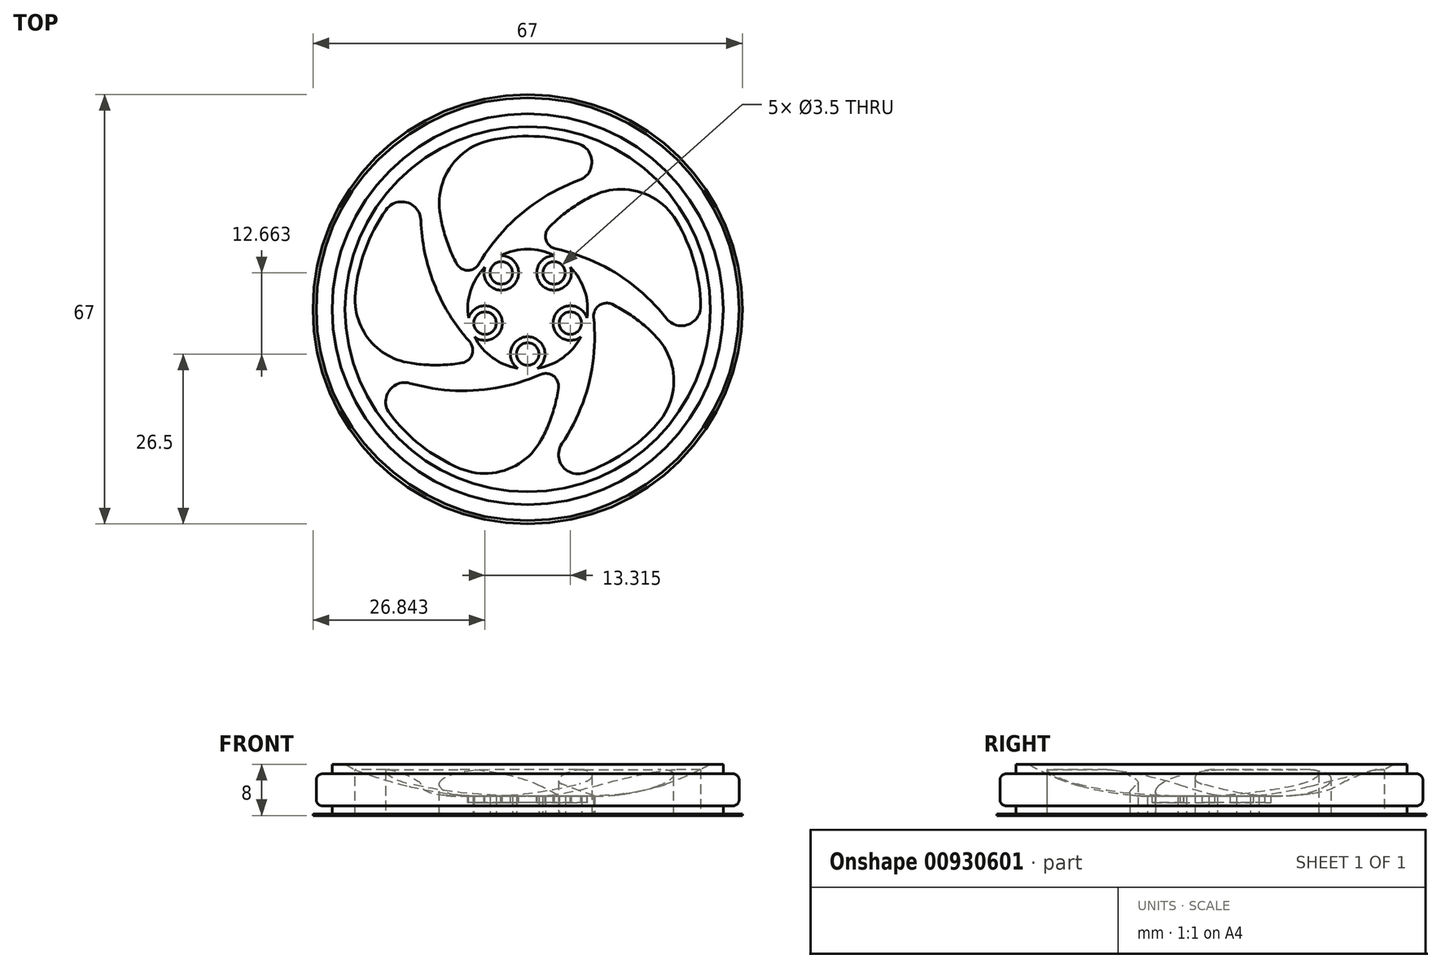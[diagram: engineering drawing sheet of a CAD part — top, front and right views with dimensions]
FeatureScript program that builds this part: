
annotation { "Feature Type Name" : "Feature", "Feature Type Description" : "" }
export const myFeature = defineFeature(function(context is Context, id is Id, definition is map)
    precondition{}
    {
        {
            var Q0;
            Q0=qCreatedBy(makeId("Front.planeOp"),FACE);
            var sketch = newSketch(context, id + "F0", { "sketchPlane" : qUnion([Q0])});
            skLineSegment(sketch, "E0.right", {"start": v(33, 1.5) * mm, "end": v(33, 6.5) * mm});
            skLineSegment(sketch, "E1", {"start": v(30.5, 6.5) * mm, "end": v(33, 6.5) * mm});
            skLineSegment(sketch, "E2", {"start": v(30.5, 6.5) * mm, "end": v(30.5, 8) * mm});
            skLineSegment(sketch, "E3.MirrorCS", {"start": v(30.5, 1.5) * mm, "end": v(30.5, 0) * mm});
            skLineSegment(sketch, "E4.MirrorCS", {"start": v(30.5, 1.5) * mm, "end": v(33, 1.5) * mm});
            skLineSegment(sketch, "E5.trimOffspring", {"start": v(28.5, 8) * mm, "end": v(30.5, 8) * mm});
            skLineSegment(sketch, "E6", {"start": v(0, 0) * mm, "end": v(30.5, 0) * mm});
            skLineSegment(sketch, "E7", {"start": v(0, 0) * mm, "end": v(0, 3) * mm});
            skLineSegment(sketch, "E8", {"start": v(0, 3) * mm, "end": v(10, 3) * mm});
            skArc(sketch, "E9", {"start": v(10, 3) * mm, "mid": v(19.58, 4.27) * mm, "end": v(28.5, 8) * mm});
            skSolve(sketch);
        }
        {
            var Q0;
            Q0=qSketchRegion(id+"F0",true);
            var Q1;
            Q1=sQuery(id+"F0.wireOp",EDGE,"E7");
            revolve(context, id + "F1", {"entities" : qUnion([Q0]), "axis" : qUnion([Q1]), "revolveType" : RevolveType.FULL});
        }
        {
            var Q0;
            Q0=makeQuery(id+"F1.opRevolve","SWEPT_EDGE",EDGE,{"disambiguationData":[OSD([sQuery(id+"F0.wireOp",EDGE,"E0.right"),sQuery(id+"F0.wireOp",EDGE,"E1")])]});
            var Q1;
            Q1=makeQuery(id+"F1.opRevolve","SWEPT_EDGE",EDGE,{"disambiguationData":[OSD([sQuery(id+"F0.wireOp",EDGE,"E0.right"),sQuery(id+"F0.wireOp",EDGE,"E4.MirrorCS")])]});
            fillet(context, id + "F2", {"entities" : qUnion([Q0, Q1]), "radius" : 1 * mm, "tangentPropagation" : true, "allowEdgeOverflow" : false});
        }
        {
            var Q0;
            Q0=makeQuery(id+"F1.opRevolve","SWEPT_FACE",FACE,{"disambiguationData":[OSD([sQuery(id+"F0.wireOp",EDGE,"E6")])]});
            var sketch = newSketch(context, id + "F3", { "sketchPlane" : qUnion([Q0])});
            skCircle(sketch, "E10", {"center": v(0, 0) * mm, "radius": 10 * mm, "construction": true});
            skCircle(sketch, "E11", {"center": v(0, 0) * mm, "radius": 28.5 * mm, "construction": true});
            skArc(sketch, "E12", {"start": v(-3, 26.83) * mm, "mid": v(-17.06, 20.93) * mm, "end": v(-25.68, 8.34) * mm});
            skArc(sketch, "E13.trimOffspring", {"start": v(-26.45, 5.44) * mm, "mid": v(-25.18, -9.76) * mm, "end": v(-15.87, -21.84) * mm});
            skArc(sketch, "E14.trimOffspring", {"start": v(18.2, -19.95) * mm, "mid": v(26.1, -6.9) * mm, "end": v(25.68, 8.34) * mm});
            skLineSegment(sketch, "E15", {"start": v(0, 28.5) * mm, "end": v(0, 0) * mm, "construction": true});
            skLineSegment(sketch, "E16", {"start": v(0, 0) * mm, "end": v(-25.68, 8.34) * mm, "construction": true});
            skLineSegment(sketch, "E17", {"start": v(0, 0) * mm, "end": v(25.68, 8.34) * mm, "construction": true});
            skLineSegment(sketch, "E18", {"start": v(0, 0) * mm, "end": v(-15.87, -21.84) * mm, "construction": true});
            skLineSegment(sketch, "E19", {"start": v(0, 0) * mm, "end": v(15.87, -21.84) * mm, "construction": true});
            skArc(sketch, "E20.trimOffspring", {"start": v(24.6, 11.14) * mm, "mid": v(14.63, 22.7) * mm, "end": v(0, 27) * mm});
            skArc(sketch, "E21.trimOffspring", {"start": v(-13.35, -23.47) * mm, "mid": v(1.5, -26.96) * mm, "end": v(15.87, -21.84) * mm});
            skCircle(sketch, "E22", {"center": v(0, 7) * mm, "radius": 1.75 * mm});
            skCircle(sketch, "E23", {"center": v(-4.11, -5.66) * mm, "radius": 1.75 * mm});
            skCircle(sketch, "E24", {"center": v(4.11, -5.66) * mm, "radius": 1.75 * mm});
            skCircle(sketch, "E25", {"center": v(6.66, 2.16) * mm, "radius": 1.75 * mm});
            skCircle(sketch, "E26", {"center": v(-6.66, 2.16) * mm, "radius": 1.75 * mm});
            skArc(sketch, "E27", {"start": v(9.77, -2.12) * mm, "mid": v(8.9, 13.79) * mm, "end": v(0, 27) * mm});
            skArc(sketch, "E28", {"start": v(1, -9.95) * mm, "mid": v(15.86, -4.2) * mm, "end": v(25.68, 8.34) * mm});
            skArc(sketch, "E29", {"start": v(-9.15, -4.03) * mm, "mid": v(0.9, -16.38) * mm, "end": v(15.87, -21.84) * mm});
            skArc(sketch, "E30", {"start": v(-6.66, 7.46) * mm, "mid": v(-15.3, -5.92) * mm, "end": v(-15.87, -21.84) * mm});
            skArc(sketch, "E31", {"start": v(5.04, 8.64) * mm, "mid": v(-10.36, 12.72) * mm, "end": v(-25.68, 8.34) * mm});
            skArc(sketch, "E32", {"start": v(-6.66, 7.46) * mm, "mid": v(-16.77, 8.6) * mm, "end": v(-26.45, 5.44) * mm});
            skArc(sketch, "E33", {"start": v(5.04, 8.64) * mm, "mid": v(3, 18.6) * mm, "end": v(-3, 26.83) * mm});
            skArc(sketch, "E34", {"start": v(9.77, -2.12) * mm, "mid": v(18.62, 2.9) * mm, "end": v(24.6, 11.14) * mm});
            skArc(sketch, "E35", {"start": v(1, -9.95) * mm, "mid": v(8.52, -16.81) * mm, "end": v(18.2, -19.95) * mm});
            skArc(sketch, "E36", {"start": v(-9.15, -4.03) * mm, "mid": v(-13.36, -13.3) * mm, "end": v(-13.35, -23.47) * mm});
            skSolve(sketch);
        }
        {
            var Q0;
            Q0=qSketchRegion(id+"F3",true);
            extrude(context, id + "F4", {"entities" : qUnion([Q0]), "operationType" : NewBodyOperationType.REMOVE, "oppositeDirection" : true, "depth" : 25 * mm});
        }
        {
            var Q0;
            Q0=makeQuery(id+"F4.boolean.opBoolean","COPY",EDGE,{"derivedFrom":makeQuery(id+"F4.opExtrude","SWEPT_EDGE",EDGE,{"disambiguationData":[OSD([sQuery(id+"F3.wireOp",EDGE,"E20.trimOffspring"),sQuery(id+"F3.wireOp",EDGE,"E27")])]})});
            var Q1;
            Q1=makeQuery(id+"F4.boolean.opBoolean","COPY",EDGE,{"derivedFrom":makeQuery(id+"F4.opExtrude","SWEPT_EDGE",EDGE,{"disambiguationData":[OSD([sQuery(id+"F3.wireOp",EDGE,"E12"),sQuery(id+"F3.wireOp",EDGE,"E31")])]})});
            var Q2;
            Q2=makeQuery(id+"F4.boolean.opBoolean","COPY",EDGE,{"derivedFrom":makeQuery(id+"F4.opExtrude","SWEPT_EDGE",EDGE,{"disambiguationData":[OSD([sQuery(id+"F3.wireOp",EDGE,"E13.trimOffspring"),sQuery(id+"F3.wireOp",EDGE,"E30")])]})});
            var Q3;
            Q3=makeQuery(id+"F4.boolean.opBoolean","COPY",EDGE,{"derivedFrom":makeQuery(id+"F4.opExtrude","SWEPT_EDGE",EDGE,{"disambiguationData":[OSD([sQuery(id+"F3.wireOp",EDGE,"E21.trimOffspring"),sQuery(id+"F3.wireOp",EDGE,"E29")])]})});
            var Q4;
            Q4=makeQuery(id+"F4.boolean.opBoolean","COPY",EDGE,{"derivedFrom":makeQuery(id+"F4.opExtrude","SWEPT_EDGE",EDGE,{"disambiguationData":[OSD([sQuery(id+"F3.wireOp",EDGE,"E14.trimOffspring"),sQuery(id+"F3.wireOp",EDGE,"E28")])]})});
            fillet(context, id + "F5", {"entities" : qUnion([Q0, Q1, Q2, Q3, Q4]), "radius" : 3 * mm, "tangentPropagation" : true, "allowEdgeOverflow" : false});
        }
        {
            var Q0;
            Q0=makeQuery(id+"F4.boolean.opBoolean","COPY",EDGE,{"derivedFrom":makeQuery(id+"F4.opExtrude","SWEPT_EDGE",EDGE,{"disambiguationData":[OSD([sQuery(id+"F3.wireOp",EDGE,"E14.trimOffspring"),sQuery(id+"F3.wireOp",EDGE,"E35")])]})});
            var Q1;
            Q1=makeQuery(id+"F4.boolean.opBoolean","COPY",EDGE,{"derivedFrom":makeQuery(id+"F4.opExtrude","SWEPT_EDGE",EDGE,{"disambiguationData":[OSD([sQuery(id+"F3.wireOp",EDGE,"E20.trimOffspring"),sQuery(id+"F3.wireOp",EDGE,"E34")])]})});
            var Q2;
            Q2=makeQuery(id+"F4.boolean.opBoolean","COPY",EDGE,{"derivedFrom":makeQuery(id+"F4.opExtrude","SWEPT_EDGE",EDGE,{"disambiguationData":[OSD([sQuery(id+"F3.wireOp",EDGE,"E12"),sQuery(id+"F3.wireOp",EDGE,"E33")])]})});
            var Q3;
            Q3=makeQuery(id+"F4.boolean.opBoolean","COPY",EDGE,{"derivedFrom":makeQuery(id+"F4.opExtrude","SWEPT_EDGE",EDGE,{"disambiguationData":[OSD([sQuery(id+"F3.wireOp",EDGE,"E13.trimOffspring"),sQuery(id+"F3.wireOp",EDGE,"E32")])]})});
            var Q4;
            Q4=makeQuery(id+"F4.boolean.opBoolean","COPY",EDGE,{"derivedFrom":makeQuery(id+"F4.opExtrude","SWEPT_EDGE",EDGE,{"disambiguationData":[OSD([sQuery(id+"F3.wireOp",EDGE,"E21.trimOffspring"),sQuery(id+"F3.wireOp",EDGE,"E36")])]})});
            fillet(context, id + "F6", {"entities" : qUnion([Q0, Q1, Q2, Q3, Q4]), "radius" : 10 * mm, "tangentPropagation" : true, "allowEdgeOverflow" : false});
        }
        {
            var Q0;
            Q0=makeQuery(id+"F4.boolean.opBoolean","COPY",EDGE,{"derivedFrom":makeQuery(id+"F4.opExtrude","SWEPT_EDGE",EDGE,{"disambiguationData":[OSD([sQuery(id+"F3.wireOp",EDGE,"E30"),sQuery(id+"F3.wireOp",EDGE,"E32")])]})});
            var Q1;
            Q1=makeQuery(id+"F4.boolean.opBoolean","COPY",EDGE,{"derivedFrom":makeQuery(id+"F4.opExtrude","SWEPT_EDGE",EDGE,{"disambiguationData":[OSD([sQuery(id+"F3.wireOp",EDGE,"E29"),sQuery(id+"F3.wireOp",EDGE,"E36")])]})});
            var Q2;
            Q2=makeQuery(id+"F4.boolean.opBoolean","COPY",EDGE,{"derivedFrom":makeQuery(id+"F4.opExtrude","SWEPT_EDGE",EDGE,{"disambiguationData":[OSD([sQuery(id+"F3.wireOp",EDGE,"E28"),sQuery(id+"F3.wireOp",EDGE,"E35")])]})});
            var Q3;
            Q3=makeQuery(id+"F4.boolean.opBoolean","COPY",EDGE,{"derivedFrom":makeQuery(id+"F4.opExtrude","SWEPT_EDGE",EDGE,{"disambiguationData":[OSD([sQuery(id+"F3.wireOp",EDGE,"E27"),sQuery(id+"F3.wireOp",EDGE,"E34")])]})});
            var Q4;
            Q4=makeQuery(id+"F4.boolean.opBoolean","COPY",EDGE,{"derivedFrom":makeQuery(id+"F4.opExtrude","SWEPT_EDGE",EDGE,{"disambiguationData":[OSD([sQuery(id+"F3.wireOp",EDGE,"E31"),sQuery(id+"F3.wireOp",EDGE,"E33")])]})});
            fillet(context, id + "F7", {"entities" : qUnion([Q0, Q1, Q2, Q3, Q4]), "radius" : 2 * mm, "tangentPropagation" : true, "allowEdgeOverflow" : false});
        }
        {
            var Q0;
            Q0=makeQuery(id+"F1.opRevolve","SWEPT_FACE",FACE,{"disambiguationData":[OSD([sQuery(id+"F0.wireOp",EDGE,"E8")])]});
            var sketch = newSketch(context, id + "F8", { "sketchPlane" : qUnion([Q0])});
            skArc(sketch, "E37", {"start": v(-6.66, 6.56) * mm, "mid": v(-2.53, 3.48) * mm, "end": v(-4.18, 8.36) * mm});
            skArc(sketch, "E38", {"start": v(4.18, 8.36) * mm, "mid": v(2.53, 3.48) * mm, "end": v(6.66, 6.56) * mm});
            skArc(sketch, "E39", {"start": v(9.25, -1.4) * mm, "mid": v(4.09, -1.33) * mm, "end": v(8.3, -4.3) * mm});
            skArc(sketch, "E40", {"start": v(1.53, -9.22) * mm, "mid": v(0, -4.3) * mm, "end": v(-1.53, -9.22) * mm});
            skArc(sketch, "E41", {"start": v(-8.3, -4.3) * mm, "mid": v(-4.09, -1.33) * mm, "end": v(-9.25, -1.4) * mm});
            skArc(sketch, "E42", {"start": v(-6.66, 6.56) * mm, "mid": v(-8.9, 2.89) * mm, "end": v(-9.25, -1.4) * mm});
            skArc(sketch, "E43.trimOffspring", {"start": v(4.18, 8.36) * mm, "mid": v(0, 9.35) * mm, "end": v(-4.18, 8.36) * mm});
            skArc(sketch, "E44.trimOffspring", {"start": v(9.25, -1.4) * mm, "mid": v(8.9, 2.89) * mm, "end": v(6.66, 6.56) * mm});
            skArc(sketch, "E45.trimOffspring", {"start": v(1.53, -9.22) * mm, "mid": v(5.5, -7.56) * mm, "end": v(8.3, -4.3) * mm});
            skArc(sketch, "E46.trimOffspring", {"start": v(-8.3, -4.3) * mm, "mid": v(-5.5, -7.56) * mm, "end": v(-1.53, -9.22) * mm});
            skSolve(sketch);
        }
        {
            var Q0;
            Q0=qSketchRegion(id+"F8",true);
            extrude(context, id + "F9", {"entities" : qUnion([Q0]), "operationType" : NewBodyOperationType.REMOVE, "oppositeDirection" : true, "depth" : 1 * mm});
        }
        {
            var Q0;
            Q0=makeQuery(id+"F1.opRevolve","SWEPT_FACE",FACE,{"disambiguationData":[OSD([sQuery(id+"F0.wireOp",EDGE,"E6")])]});
            var sketch = newSketch(context, id + "F10", { "sketchPlane" : qUnion([Q0])});
            skCircle(sketch, "E47", {"center": v(0, 0) * mm, "radius": 33.5 * mm});
            skCircle(sketch, "E48", {"center": v(0, 0) * mm, "radius": 30.5 * mm});
            skSolve(sketch);
        }
        {
            var Q0;
            Q0=qSketchRegion(id+"F10",true);
            extrude(context, id + "F11", {"entities" : qUnion([Q0]), "operationType" : NewBodyOperationType.ADD, "oppositeDirection" : true, "depth" : 0.2 * mm, "offsetDistance" : 25 * mm});
        }
    });
